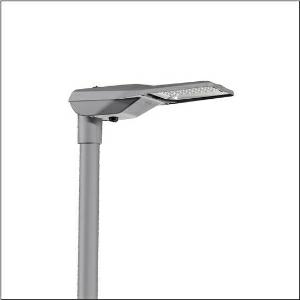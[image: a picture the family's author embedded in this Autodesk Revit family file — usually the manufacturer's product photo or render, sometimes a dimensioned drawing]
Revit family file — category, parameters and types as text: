
# Revit family: streetlight_sl_21_iq_mini___st1_0a_5xe2d31y08gb_99d1
name_source: partatom
category: Lighting Fixtures
units: mm (PartAtom-declared; Revit-internal decimal feet)

## family parameters
Cut with Voids When Loaded = No
Host = Face
Light Source = No
Part Type = Normal
Room Calculation Point = No
Round Connector Dimension = Use Diameter
Shared = No

## types (1)
- --- (1 x LED, 5990 lm, 39.8 W, 3000K)
    Apparent Load = 40 VA
    CIE Flux Codes = 37 72 97 100 100
    Color Rendering = 70
    Color Temperature = 3000K
    Default Elevation = 1800 mm
    Description = Streetlight SL 21 iQ mini, mast luminaire, primary light control with lens, of PMMA, primary optical cover: cover, of toughened safety glass, transparent, light distribution: ST1.0a, light emission: direct distribution, primary light characteristic: asymmetric, installation type: post-top, side-entry, LED, High Power LED, rated luminous flux: 5.990lm, luminous efficacy: 151lm/W, light colour: 730, colour temperature: 3000K, control gear: iQ-Street Remote, D4i with power reduction, control: pre-setting: logarithmic dimming characteristic, Street-Remote, Auto-Match, Temp-Guard, Lumen-Switch, Night-Set, Smart-Wire, Light-Fading, Desk-Remote (wireless, voltage-free reading and setting of iQ features in the workshop via application-optimized NFC function/RFID function), optimised constant luminous flux control (CLO 2.0), mains connection: 220..240V, AC, 50/60Hz, start of lifetime: 40W, end of service life: 41W, reduction: 18W, luminaire housing, of diecast aluminium, powder-coated, SITECO metallic grey (DB 702S), corrosivity category C5 high according to DIN EN ISO 12944, please order mast flange separately, inclination adjustable: 0°, 5°, 10°, 15°, sealing non-destructively replaceable, multi-level sealing system, length: 628mm, width: 235mm, height: 110mm, mast flange for spigot size: 42mm (side-entry): 5XC10008XM4, 60/48mm (side-entry/post-top): 5XC10108XM2, 76/60mm (side-entry/post-top): 5XC10108XM1, mounting height: 4..8m, Smart Interface below and above, protection rating (complete): IP66, insulation class (complete): insulation class II (safety insulation), certification: CE, ENEC, ENEC+, VDE, impact resistance: IK10, permissible operating ambient temperature for outdoor applications: -40..+50°C, standard-compliant lighting for roads and squares, packaging unit: 1 piece

Light Distribution: ST1.0a
    Height = 110 mm
    Lamp = 1 x LED
    Lamp Light Flux = 5990 lm
    Lamp Power = 39.8 W
    Lamp count = 1
    Length = 625 mm
    Luminous efficacy = 151 lm/W
    Manufacturer = Siteco
    ModVariant = No
    Model = 5XE2D31Y08GB
    Number of Poles = 1
    OnlyDefault = Yes
    Power Factor = 1
    Product Name = Streetlight SL 21 iQ mini | ST1.0a
    Product group = mast luminaire | pylon top
    ProductGroupID = 6100
    Protection Class = Protection class II
    Protection Degree = IP 66
    RLX_Detail_Level = 1
    RLX_Emergency_Light_Flux = 0 lm
    RLX_Emergency_Type = 0
    RLX_Emergency_Type_DB = No
    RlxData = <blob elided: 92933 chars, md5=328f9cd6>
    Socket = socket
    Standby Power = 0 W
    System Light Flux = 5990 lm
    System Power = 40 W
    Type Comments = factory setting: luminous flux: 100 % | dim-lin: 254 | 800 mA
    Type Image = l_1003514.jpg
    URL = http://relux.com
    VarID = @adj_115037
    Voltage = 0 V
    Weight = 0.00 kg
    Width = 234 mm

## geometry (parser evidence)
native form markers: Blend x4, Sweep x11
no freeform markers — native parametric forms only
